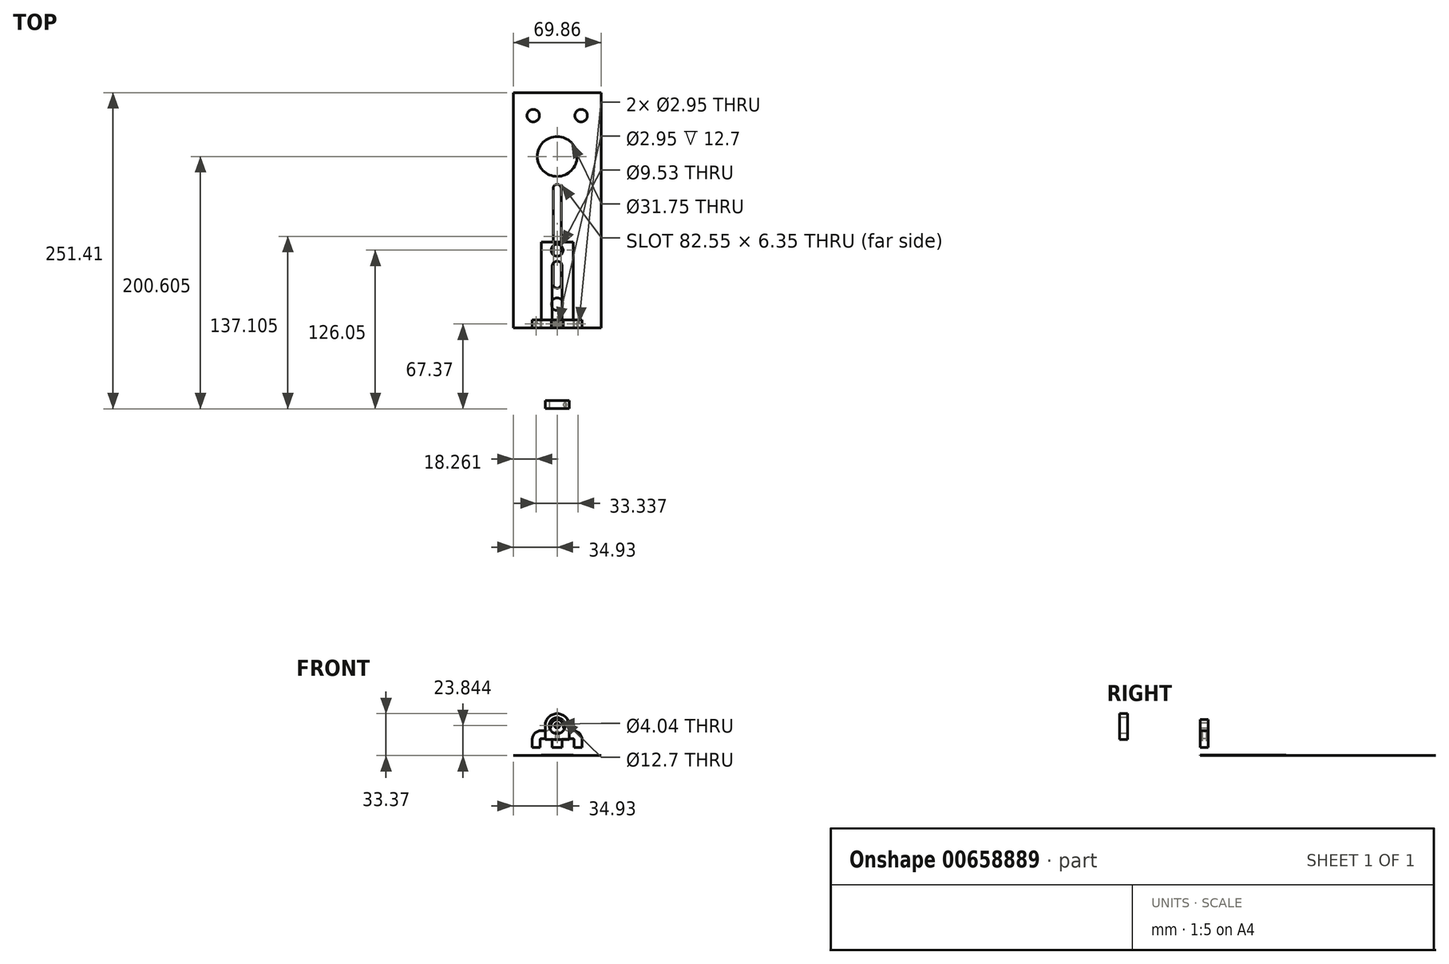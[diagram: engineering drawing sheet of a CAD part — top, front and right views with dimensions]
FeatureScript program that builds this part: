
annotation { "Feature Type Name" : "Feature", "Feature Type Description" : "" }
export const myFeature = defineFeature(function(context is Context, id is Id, definition is map)
    precondition{}
    {
        {
            assignVariable(context, id + "F0", {"name" : "baseThickness", "anyValue" : 0.25});
        }
        {
            assignVariable(context, id + "F1", {"name" : "topThickness", "anyValue" : 0.25});
        }
        {
            var Q0;
            Q0=qCreatedBy(makeId("Top.planeOp"),FACE);
            var sketch = newSketch(context, id + "F2", { "sketchPlane" : qUnion([Q0])});
            skLineSegment(sketch, "E0.bottom", {"start": v(-34.92, 93.6) * mm, "end": v(34.92, 93.6) * mm});
            skLineSegment(sketch, "E0.top", {"start": v(-34.92, -93.6) * mm, "end": v(34.92, -93.6) * mm});
            skLineSegment(sketch, "E0.left", {"start": v(-34.92, 93.6) * mm, "end": v(-34.92, -93.6) * mm});
            skLineSegment(sketch, "E0.right", {"start": v(34.93, 93.6) * mm, "end": v(34.93, -93.6) * mm});
            skCircle(sketch, "E1", {"center": v(0, 42.8) * mm, "radius": 15.88 * mm});
            skCircle(sketch, "E2", {"center": v(-19.05, 75.32) * mm, "radius": 2.15 * mm});
            skCircle(sketch, "E3", {"center": v(19.05, 75.32) * mm, "radius": 2.15 * mm});
            skArc(sketch, "E4", {"start": v(3.17, 17.4) * mm, "mid": v(0, 20.58) * mm, "end": v(-3.17, 17.4) * mm});
            skArc(sketch, "E5", {"start": v(-3.18, -58.8) * mm, "mid": v(0, -61.97) * mm, "end": v(3.18, -58.8) * mm});
            skLineSegment(sketch, "E6", {"start": v(-3.18, 17.4) * mm, "end": v(-3.18, -58.8) * mm});
            skLineSegment(sketch, "E7", {"start": v(3.17, -58.8) * mm, "end": v(3.17, 17.4) * mm});
            skCircle(sketch, "E8", {"center": v(0, -74.67) * mm, "radius": 2.15 * mm});
            skCircle(sketch, "E9", {"center": v(0, -90.43) * mm, "radius": 1.47 * mm});
            skSolve(sketch);
        }
        {
            var Q0;
            Q0=makeQuery(id+"F2.imprint","IMPRINT",FACE,{"disambiguationData":[TD([[makeQuery(id+"F2.imprint","IMPRINT",EDGE,{"derivedFrom":sQuery(id+"F2.wireOp",EDGE,"E0.bottom")}),-1.0]])]});
            extrude(context, id + "F3", {"entities" : qUnion([Q0]), "depth" : (getVariable(context, 'baseThickness')) * mm, "offsetDistance" : 25.4 * mm});
        }
        {
            var Q0;
            Q0=makeQuery(id+"F3.opExtrude","CAP_FACE",FACE,{"disambiguationData":[OSD([sQuery(id+"F2.wireOp",EDGE,"E0.bottom"),sQuery(id+"F2.wireOp",EDGE,"E0.top"),sQuery(id+"F2.wireOp",EDGE,"E0.left"),sQuery(id+"F2.wireOp",EDGE,"E0.right"),sQuery(id+"F2.wireOp",EDGE,"E1"),sQuery(id+"F2.wireOp",EDGE,"E2"),sQuery(id+"F2.wireOp",EDGE,"E3"),sQuery(id+"F2.wireOp",EDGE,"E4"),sQuery(id+"F2.wireOp",EDGE,"E5"),sQuery(id+"F2.wireOp",EDGE,"E6"),sQuery(id+"F2.wireOp",EDGE,"E7"),sQuery(id+"F2.wireOp",EDGE,"E8"),sQuery(id+"F2.wireOp",EDGE,"E9")])],"isStart":false});
            var sketch = newSketch(context, id + "F4", { "sketchPlane" : qUnion([Q0])});
            skLineSegment(sketch, "E10.bottom", {"start": v(-12.7, -25.4) * mm, "end": v(12.7, -25.4) * mm});
            skLineSegment(sketch, "E10.top", {"start": v(-12.7, -157.8) * mm, "end": v(12.7, -157.8) * mm});
            skLineSegment(sketch, "E10.left", {"start": v(-12.7, -25.4) * mm, "end": v(-12.7, -157.8) * mm});
            skLineSegment(sketch, "E10.right", {"start": v(12.7, -25.4) * mm, "end": v(12.7, -157.8) * mm});
            skArc(sketch, "E11", {"start": v(3.97, -44.45) * mm, "mid": v(0, -40.48) * mm, "end": v(-3.97, -44.45) * mm});
            skArc(sketch, "E12", {"start": v(-3.97, -143.51) * mm, "mid": v(0, -147.48) * mm, "end": v(3.97, -143.51) * mm});
            skLineSegment(sketch, "E13", {"start": v(-3.97, -143.51) * mm, "end": v(-3.97, -44.45) * mm});
            skLineSegment(sketch, "E14", {"start": v(3.97, -44.45) * mm, "end": v(3.97, -143.51) * mm});
            skPoint(sketch, "E15", {"position": v(0, -25.4) * mm});
            skPoint(sketch, "E16", {"position": v(0, -93.6) * mm});
            skCircle(sketch, "E17", {"center": v(0, -31.75) * mm, "radius": 4.76 * mm});
            skPoint(sketch, "E18", {"position": v(0, -61.97) * mm});
            skCircle(sketch, "E19", {"center": v(-6.35, -154.62) * mm, "radius": 1.47 * mm});
            skCircle(sketch, "E20.MirrorC", {"center": v(6.35, -154.62) * mm, "radius": 1.47 * mm});
            skSolve(sketch);
        }
        {
            var Q0;
            Q0 = qSketchRegion(id + "F4", true);
            extrude(context, id + "F5", {"entities" : qUnion([Q0]), "depth" : (getVariable(context, 'topThickness')) * mm, "offsetDistance" : 25.4 * mm});
        }
        {
            var Q0;
            Q0=makeQuery(id+"F3.opExtrude","SWEPT_FACE",FACE,{"disambiguationData":[OSD([sQuery(id+"F2.wireOp",EDGE,"E0.top")])]});
            var sketch = newSketch(context, id + "F6", { "sketchPlane" : qUnion([Q0])});
            skArc(sketch, "E21", {"start": v(4.76, 23.84) * mm, "mid": v(0, 28.6) * mm, "end": v(-4.76, 23.84) * mm});
            skLineSegment(sketch, "E22", {"start": v(-4.76, 23.84) * mm, "end": v(-4.76, 23.84) * mm});
            skCircle(sketch, "E23", {"center": v(0, 23.84) * mm, "radius": 2.02 * mm});
            skLineSegment(sketch, "E24", {"start": v(-8.76, 19.84) * mm, "end": v(-12.7, 19.84) * mm});
            skLineSegment(sketch, "E25", {"start": v(-19.84, 12.7) * mm, "end": v(-19.84, 6.35) * mm});
            skLineSegment(sketch, "E26", {"start": v(-19.84, 6.35) * mm, "end": v(-13.5, 6.35) * mm});
            skLineSegment(sketch, "E27", {"start": v(-13.5, 6.35) * mm, "end": v(-13.5, 12.7) * mm});
            skLineSegment(sketch, "E28", {"start": v(-12.7, 13.5) * mm, "end": v(-4.29, 13.5) * mm});
            skPoint(sketch, "E29.visualSharp", {"position": v(-4.76, 19.84) * mm});
            skArc(sketch, "E29.filletArc", {"start": v(-8.76, 19.84) * mm, "mid": v(-5.93, 21.02) * mm, "end": v(-4.76, 23.84) * mm});
            skLineSegment(sketch, "E30", {"start": v(-3.9, 13.1) * mm, "end": v(-3.9, 6.35) * mm});
            skLineSegment(sketch, "E31", {"start": v(-3.9, 6.35) * mm, "end": v(0, 6.35) * mm});
            skPoint(sketch, "E32.visualSharp", {"position": v(-19.84, 19.84) * mm});
            skArc(sketch, "E32.filletArc", {"start": v(-12.7, 19.84) * mm, "mid": v(-17.75, 17.75) * mm, "end": v(-19.84, 12.7) * mm});
            skLineSegment(sketch, "E33.MirrorCS", {"start": v(4.76, 23.84) * mm, "end": v(4.76, 23.84) * mm});
            skPoint(sketch, "E34.MirrorP", {"position": v(4.76, 19.84) * mm});
            skArc(sketch, "E35.MirrorCS", {"start": v(8.76, 19.84) * mm, "mid": v(5.93, 21.02) * mm, "end": v(4.76, 23.84) * mm});
            skLineSegment(sketch, "E36.MirrorCS", {"start": v(8.76, 19.84) * mm, "end": v(12.7, 19.84) * mm});
            skArc(sketch, "E37.MirrorCS", {"start": v(12.7, 19.84) * mm, "mid": v(17.75, 17.75) * mm, "end": v(19.84, 12.7) * mm});
            skLineSegment(sketch, "E38.MirrorCS", {"start": v(19.84, 12.7) * mm, "end": v(19.84, 6.35) * mm});
            skLineSegment(sketch, "E39.MirrorCS", {"start": v(3.9, 6.35) * mm, "end": v(0, 6.35) * mm});
            skLineSegment(sketch, "E40.MirrorCS", {"start": v(19.84, 6.35) * mm, "end": v(13.5, 6.35) * mm});
            skPoint(sketch, "E41.visualSharp", {"position": v(-13.5, 13.5) * mm});
            skArc(sketch, "E41.filletArc", {"start": v(-12.7, 13.5) * mm, "mid": v(-13.26, 13.26) * mm, "end": v(-13.5, 12.7) * mm});
            skArc(sketch, "E42.MirrorCS", {"start": v(12.7, 13.5) * mm, "mid": v(13.26, 13.26) * mm, "end": v(13.5, 12.7) * mm});
            skLineSegment(sketch, "E43.MirrorCS", {"start": v(13.5, 6.35) * mm, "end": v(13.5, 12.7) * mm});
            skLineSegment(sketch, "E44", {"start": v(-9.68, 19.84) * mm, "end": v(-9.68, 13.5) * mm, "construction": true});
            skPoint(sketch, "E45.visualSharp", {"position": v(-3.9, 13.5) * mm});
            skArc(sketch, "E45.filletArc", {"start": v(-3.9, 13.1) * mm, "mid": v(-4, 13.38) * mm, "end": v(-4.29, 13.5) * mm});
            skLineSegment(sketch, "E46.MirrorCS", {"start": v(3.9, 13.1) * mm, "end": v(3.9, 6.35) * mm});
            skArc(sketch, "E47.MirrorCS", {"start": v(3.9, 13.1) * mm, "mid": v(4, 13.38) * mm, "end": v(4.29, 13.5) * mm});
            skLineSegment(sketch, "E48.MirrorCS", {"start": v(12.7, 13.5) * mm, "end": v(4.29, 13.5) * mm});
            skSolve(sketch);
        }
        {
            var Q0;
            Q0 = qSketchRegion(id + "F6", true);
            extrude(context, id + "F7", {"entities" : qUnion([Q0]), "oppositeDirection" : true, "depth" : 6.35 * mm, "offsetDistance" : 25.4 * mm});
        }
        {
            var Q0;
            Q0=makeQuery(id+"F5.opExtrude","SWEPT_FACE",FACE,{"disambiguationData":[OSD([sQuery(id+"F4.wireOp",EDGE,"E10.top")])]});
            var sketch = newSketch(context, id + "F8", { "sketchPlane" : qUnion([Q0])});
            skLineSegment(sketch, "E49.bottom", {"start": v(-9.53, 12.7) * mm, "end": v(9.53, 12.7) * mm});
            skLineSegment(sketch, "E49.left", {"start": v(-9.53, 12.7) * mm, "end": v(-9.53, 23.84) * mm});
            skLineSegment(sketch, "E49.right", {"start": v(9.53, 12.7) * mm, "end": v(9.53, 23.84) * mm});
            skArc(sketch, "E50", {"start": v(9.53, 23.84) * mm, "mid": v(0, 33.37) * mm, "end": v(-9.53, 23.84) * mm});
            skCircle(sketch, "E51", {"center": v(0, 23.84) * mm, "radius": 6.35 * mm});
            skSolve(sketch);
        }
        {
            var Q0;
            Q0 = qSketchRegion(id + "F8", true);
            extrude(context, id + "F9", {"entities" : qUnion([Q0]), "oppositeDirection" : true, "depth" : 6.35 * mm, "offsetDistance" : 25.4 * mm});
        }
        {
            var Q0;
            Q0=makeQuery(id+"F7.opExtrude","SWEPT_FACE",FACE,{"disambiguationData":[OSD([sQuery(id+"F6.wireOp",EDGE,"E26")])]});
            var sketch = newSketch(context, id + "F10", { "sketchPlane" : qUnion([Q0])});
            skCircle(sketch, "E52", {"center": v(-16.67, 90.43) * mm, "radius": 1.47 * mm});
            skCircle(sketch, "E53", {"center": v(16.67, 90.43) * mm, "radius": 1.47 * mm});
            skLineSegment(sketch, "E54", {"start": v(-19.84, 87.26) * mm, "end": v(-13.5, 93.6) * mm, "construction": true});
            skLineSegment(sketch, "E55", {"start": v(-13.5, 87.26) * mm, "end": v(-19.84, 93.6) * mm, "construction": true});
            skLineSegment(sketch, "E56", {"start": v(19.84, 87.26) * mm, "end": v(13.5, 93.6) * mm, "construction": true});
            skLineSegment(sketch, "E57", {"start": v(19.84, 93.6) * mm, "end": v(13.5, 87.26) * mm, "construction": true});
            skSolve(sketch);
        }
        {
            var Q0;
            Q0 = qSketchRegion(id + "F10", true);
            extrude(context, id + "F11", {"entities" : qUnion([Q0]), "operationType" : NewBodyOperationType.REMOVE, "endBound" : BoundingType.THROUGH_ALL, "depth" : 25.4 * mm, "offsetDistance" : 25.4 * mm});
        }
        {
            var Q0;
            Q0=sQuery(id+"F2.wireOp",VERTEX,"E3.center");
            var Q1;
            Q1=sQuery(id+"F2.wireOp",VERTEX,"E2.center");
            var Q2;
            Q2=sQuery(id+"F2.wireOp",VERTEX,"E8.center");
            var Q3;
            Q3=makeQuery(id+"F3.opExtrude","SWEPT_BODY",BODY,{"disambiguationData":[OSD([sQuery(id+"F2.wireOp",EDGE,"E0.bottom"),sQuery(id+"F2.wireOp",EDGE,"E0.top"),sQuery(id+"F2.wireOp",EDGE,"E0.left"),sQuery(id+"F2.wireOp",EDGE,"E0.right"),sQuery(id+"F2.wireOp",EDGE,"E1"),sQuery(id+"F2.wireOp",EDGE,"E2"),sQuery(id+"F2.wireOp",EDGE,"E3"),sQuery(id+"F2.wireOp",EDGE,"E4"),sQuery(id+"F2.wireOp",EDGE,"E5"),sQuery(id+"F2.wireOp",EDGE,"E6"),sQuery(id+"F2.wireOp",EDGE,"E7"),sQuery(id+"F2.wireOp",EDGE,"E8"),sQuery(id+"F2.wireOp",EDGE,"E9")])]});
            hole(context, id + "F12", {"style" : HoleStyle.C_SINK, "endStyle" : HoleEndStyle.THROUGH, "oppositeDirection" : true, "standardTappedOrClearance" : lookupTablePath({ "standard" : "ANSI", "fit" : "Close", "size" : "#10", "type" : "Clearance" }), "standardBlindInLast" : lookupTablePath({ "fit" : "Close", "standard" : "ANSI", "size" : "#10", "type" : "Clearance" }), "holeDiameter" : 4.98 * mm, "cSinkDiameter" : 10.44 * mm, "cSinkAngle" : 82 * degree, "majorDiameter" : 7.94 * mm, "isTappedThrough" : true, "tappedDepth" : 12.7 * mm, "tapClearance" : 3, "locations" : qUnion([Q0, Q1, Q2]), "scope" : qUnion([Q3])});
        }
        {
            var Q0;
            Q0=sQuery(id+"F2.wireOp",VERTEX,"E9.center");
            var Q1;
            Q1=makeQuery(id+"F3.opExtrude","SWEPT_BODY",BODY,{"disambiguationData":[OSD([sQuery(id+"F2.wireOp",EDGE,"E0.bottom"),sQuery(id+"F2.wireOp",EDGE,"E0.top"),sQuery(id+"F2.wireOp",EDGE,"E0.left"),sQuery(id+"F2.wireOp",EDGE,"E0.right"),sQuery(id+"F2.wireOp",EDGE,"E1"),sQuery(id+"F2.wireOp",EDGE,"E2"),sQuery(id+"F2.wireOp",EDGE,"E3"),sQuery(id+"F2.wireOp",EDGE,"E4"),sQuery(id+"F2.wireOp",EDGE,"E5"),sQuery(id+"F2.wireOp",EDGE,"E6"),sQuery(id+"F2.wireOp",EDGE,"E7"),sQuery(id+"F2.wireOp",EDGE,"E8"),sQuery(id+"F2.wireOp",EDGE,"E9")])]});
            hole(context, id + "F13", {"style" : HoleStyle.C_SINK, "endStyle" : HoleEndStyle.THROUGH, "oppositeDirection" : true, "standardTappedOrClearance" : lookupTablePath({ "standard" : "ANSI", "fit" : "Close", "size" : "#4", "type" : "Clearance" }), "standardBlindInLast" : lookupTablePath({ "fit" : "Close", "standard" : "ANSI", "size" : "#4", "type" : "Clearance" }), "holeDiameter" : 2.95 * mm, "cSinkDiameter" : 6.48 * mm, "cSinkAngle" : 82 * degree, "majorDiameter" : 6.35 * mm, "isTappedThrough" : true, "tappedDepth" : 12.7 * mm, "tapClearance" : 3, "locations" : qUnion([Q0]), "scope" : qUnion([Q1])});
        }
        {
            var Q0;
            Q0=makeQuery(id+"F4.imprint","IMPRINT",FACE,{"disambiguationData":[TD([[makeQuery(id+"F4.imprint","IMPRINT",EDGE,{"derivedFrom":sQuery(id+"F4.wireOp",EDGE,"E20.MirrorC")}),-1.0]])]});
            var Q1;
            Q1=makeQuery(id+"F4.imprint","IMPRINT",FACE,{"disambiguationData":[TD([[makeQuery(id+"F4.imprint","IMPRINT",EDGE,{"derivedFrom":sQuery(id+"F4.wireOp",EDGE,"E19")}),1.0]])]});
            extrude(context, id + "F14", {"entities" : qUnion([Q0, Q1]), "operationType" : NewBodyOperationType.REMOVE, "depth" : 12.7 * mm, "offsetDistance" : 25.4 * mm});
        }
        {
            var Q0;
            Q0=makeQuery(id+"F2.imprint","IMPRINT",FACE,{"disambiguationData":[TD([[makeQuery(id+"F2.imprint","IMPRINT",EDGE,{"derivedFrom":sQuery(id+"F2.wireOp",EDGE,"E9")}),1.0]])]});
            extrude(context, id + "F15", {"entities" : qUnion([Q0]), "operationType" : NewBodyOperationType.REMOVE, "depth" : 19.05 * mm, "offsetDistance" : 25.4 * mm});
        }
    });
